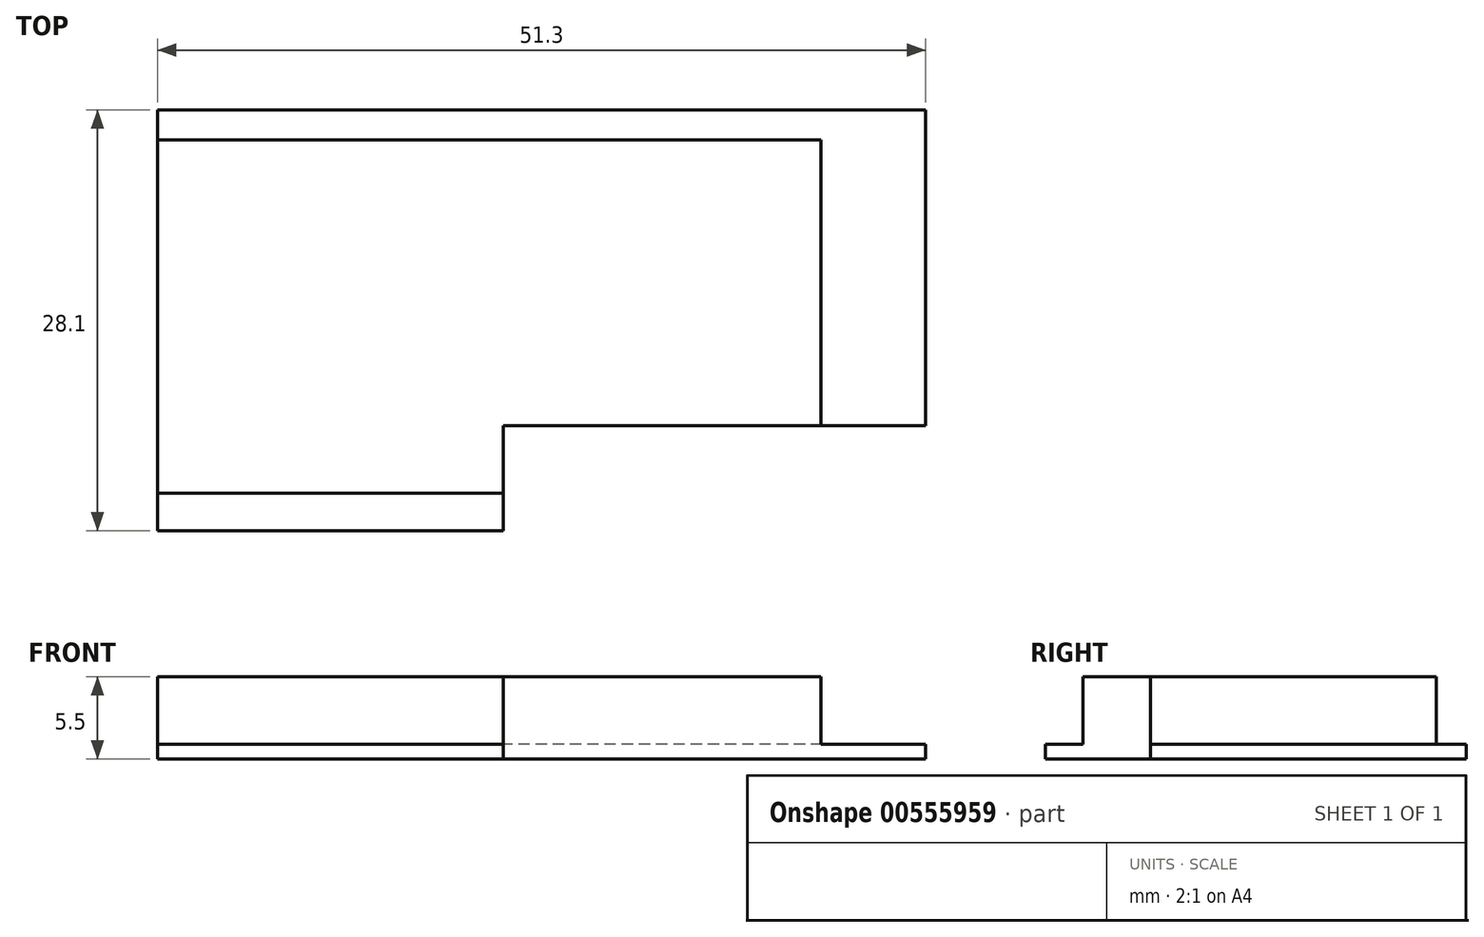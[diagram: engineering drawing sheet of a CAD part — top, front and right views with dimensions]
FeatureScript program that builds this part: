
annotation { "Feature Type Name" : "Feature", "Feature Type Description" : "" }
export const myFeature = defineFeature(function(context is Context, id is Id, definition is map)
    precondition{}
    {
        {
            var Q0;
            Q0=qCreatedBy(makeId("Top.planeOp"),FACE);
            var sketch = newSketch(context, id + "F0", { "sketchPlane" : qUnion([Q0])});
            skLineSegment(sketch, "E0.bottom", {"start": v(25.65, -10.55) * mm, "end": v(-2.55, -10.55) * mm});
            skLineSegment(sketch, "E0.top", {"start": v(25.65, 10.55) * mm, "end": v(-25.65, 10.55) * mm});
            skLineSegment(sketch, "E0.left", {"start": v(25.65, -10.55) * mm, "end": v(25.65, 10.55) * mm});
            skLineSegment(sketch, "E0.right", {"start": v(-25.65, -10.55) * mm, "end": v(-25.65, 10.55) * mm});
            skPoint(sketch, "E0.middle", {"position": v(0, 0) * mm});
            skLineSegment(sketch, "E1.bottom", {"start": v(-25.65, 10.55) * mm, "end": v(-2.55, 10.55) * mm});
            skLineSegment(sketch, "E1.top", {"start": v(-25.65, -17.55) * mm, "end": v(-2.55, -17.55) * mm});
            skLineSegment(sketch, "E1.left", {"start": v(-25.65, 10.55) * mm, "end": v(-25.65, -17.55) * mm});
            skLineSegment(sketch, "E1.right", {"start": v(-2.55, -10.55) * mm, "end": v(-2.55, -17.55) * mm});
            skSolve(sketch);
        }
        {
            var Q0;
            Q0=makeQuery(id+"F0.imprint","IMPRINT",FACE,{"disambiguationData":[TD([[makeQuery(id+"F0.imprint","IMPRINT",EDGE,{"derivedFrom":sQuery(id+"F0.wireOp",EDGE,"E0.bottom")}),-1.0]])]});
            extrude(context, id + "F1", {"entities" : qUnion([Q0]), "depth" : 1 * mm, "offsetDistance" : 25 * mm});
        }
        {
            var Q0;
            Q0=makeQuery(id+"F1.opExtrude","CAP_FACE",FACE,{"disambiguationData":[OSD([sQuery(id+"F0.wireOp",EDGE,"E0.bottom"),sQuery(id+"F0.wireOp",EDGE,"E0.top"),sQuery(id+"F0.wireOp",EDGE,"E0.left"),sQuery(id+"F0.wireOp",EDGE,"E1.bottom"),sQuery(id+"F0.wireOp",EDGE,"E1.top"),sQuery(id+"F0.wireOp",EDGE,"E1.left"),sQuery(id+"F0.wireOp",EDGE,"E1.right")])],"isStart":false});
            var sketch = newSketch(context, id + "F2", { "sketchPlane" : qUnion([Q0])});
            skLineSegment(sketch, "E2", {"start": v(18.65, 8.55) * mm, "end": v(18.65, -10.55) * mm});
            skLineSegment(sketch, "E3", {"start": v(18.65, 8.55) * mm, "end": v(-25.65, 8.55) * mm});
            skLineSegment(sketch, "E4", {"start": v(-25.65, -15.05) * mm, "end": v(-2.55, -15.05) * mm});
            skSolve(sketch);
        }
        {
            var Q0;
            {var subQ3=sQuery(id+"F2.wireOp",EDGE,"E2");Q0=makeQuery(id+"F2.imprint","IMPRINT",FACE,{"disambiguationData":[TD([[makeQuery(id+"F2.imprint","IMPRINT",EDGE,{"derivedFrom":subQ3}),-1.0]])]});}
            extrude(context, id + "F3", {"entities" : qUnion([Q0]), "operationType" : NewBodyOperationType.ADD, "depth" : 4.5 * mm, "offsetDistance" : 25 * mm});
        }
    });
